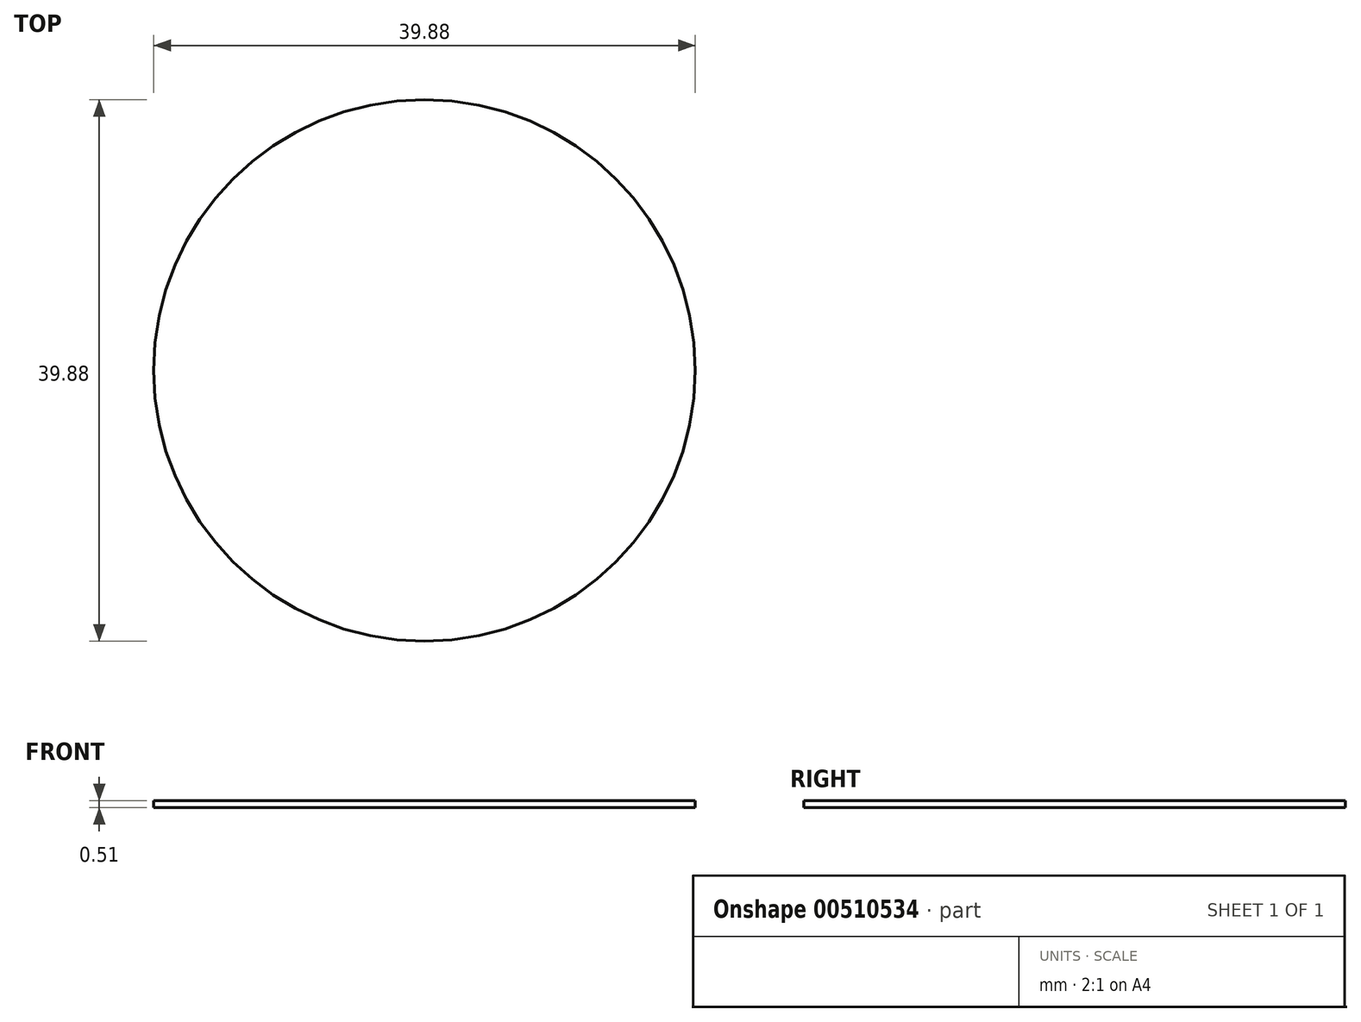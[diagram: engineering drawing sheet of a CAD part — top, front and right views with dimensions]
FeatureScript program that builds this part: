
annotation { "Feature Type Name" : "Feature", "Feature Type Description" : "" }
export const myFeature = defineFeature(function(context is Context, id is Id, definition is map)
    precondition{}
    {
        {
            var Q0;
            Q0=qCreatedBy(makeId("Top.planeOp"),FACE);
            var sketch = newSketch(context, id + "F0", { "sketchPlane" : qUnion([Q0])});
            skCircle(sketch, "E0", {"center": v(0, 0) * mm, "radius": 19.69 * mm});
            skCircle(sketch, "E1", {"center": v(0, 0) * mm, "radius": 19.94 * mm});
            skSolve(sketch);
        }
        {
            var Q0;
            Q0 = qSketchRegion(id + "F0", true);
            var Q1;
            Q1=makeQuery(id+"F0.imprint","IMPRINT",FACE,{"disambiguationData":[TD([[makeQuery(id+"F0.imprint","IMPRINT",EDGE,{"derivedFrom":sQuery(id+"F0.wireOp",EDGE,"E0")}),1.0]])]});
            extrude(context, id + "F1", {"entities" : qUnion([Q0, Q1]), "depth" : 0.5 * mm, "offsetDistance" : 25.4 * mm});
        }
        {
            var Q0;
            Q0=makeQuery(id+"F0.imprint","IMPRINT",FACE,{"disambiguationData":[TD([[makeQuery(id+"F0.imprint","IMPRINT",EDGE,{"derivedFrom":sQuery(id+"F0.wireOp",EDGE,"E0")}),1.0]])]});
            extrude(context, id + "F2", {"entities" : qUnion([Q0]), "operationType" : NewBodyOperationType.ADD, "depth" : 0.03 * mm, "offsetDistance" : 25.4 * mm});
        }
    });
